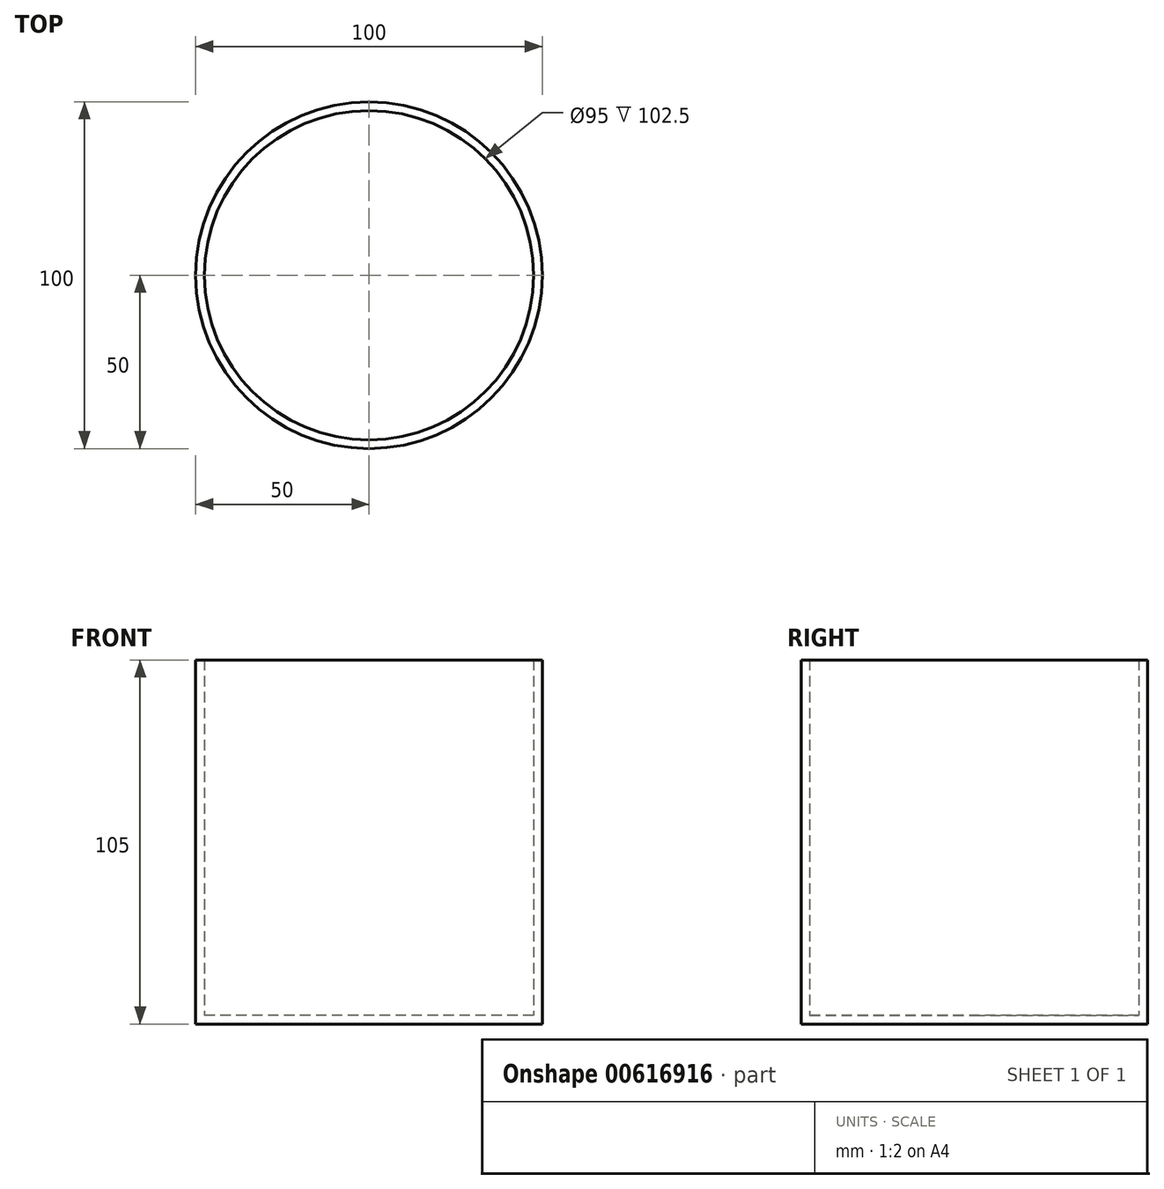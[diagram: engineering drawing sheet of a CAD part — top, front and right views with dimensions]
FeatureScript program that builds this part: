
annotation { "Feature Type Name" : "Feature", "Feature Type Description" : "" }
export const myFeature = defineFeature(function(context is Context, id is Id, definition is map)
    precondition{}
    {
        {
            var Q0;
            Q0=qCreatedBy(makeId("Top.planeOp"),FACE);
            var sketch = newSketch(context, id + "F0", { "sketchPlane" : qUnion([Q0])});
            skCircle(sketch, "E0", {"center": v(0, 0) * mm, "radius": 50 * mm});
            skSolve(sketch);
        }
        {
            var Q0;
            Q0=makeQuery(id+"F0.imprint","IMPRINT",FACE,{"disambiguationData":[TD([[makeQuery(id+"F0.imprint","IMPRINT",EDGE,{"derivedFrom":sQuery(id+"F0.wireOp",EDGE,"E0")}),1.0]])]});
            extrude(context, id + "F1", {"entities" : qUnion([Q0]), "depth" : 105 * mm, "offsetDistance" : 25 * mm});
        }
        {
            var Q0;
            Q0=qCreatedBy(makeId("Right.planeOp"),FACE);
            cPlane(context, id + "F2", {"entities" : qUnion([Q0]), "cplaneType" : CPlaneType.OFFSET, "offset" : 50 * mm, "width" : 150 * mm, "height" : 150 * mm});
        }
        {
            var Q0;
            Q0=makeQuery(id+"F1.opExtrude","CAP_FACE",FACE,{"disambiguationData":[OSD([sQuery(id+"F0.wireOp",EDGE,"E0")])],"isStart":false});
            shell(context, id + "F3", {"entities" : qUnion([Q0]), "thickness" : 2.5 * mm});
        }
    });
